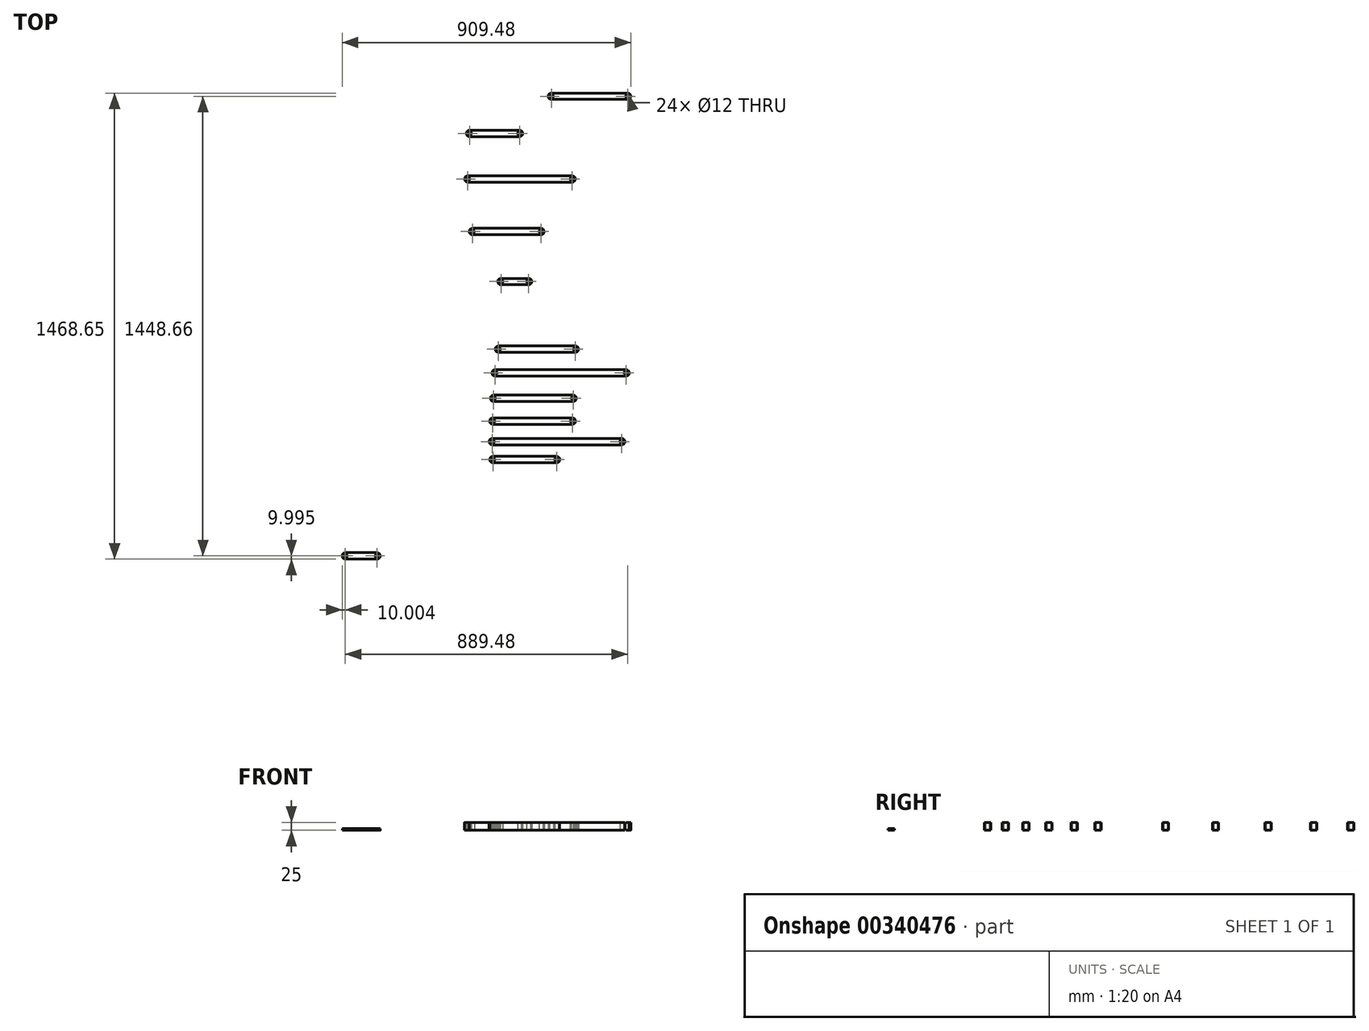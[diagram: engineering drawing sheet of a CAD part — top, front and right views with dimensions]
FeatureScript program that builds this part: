
annotation { "Feature Type Name" : "Feature", "Feature Type Description" : "" }
export const myFeature = defineFeature(function(context is Context, id is Id, definition is map)
    precondition{}
    {
        {
            var Q0;
            Q0=qCreatedBy(makeId("Top.planeOp"),FACE);
            var sketch = newSketch(context, id + "F0", { "sketchPlane" : qUnion([Q0])});
            skLineSegment(sketch, "E0", {"start": v(-54.16, 16.37) * mm, "end": v(146.43, 16.37) * mm, "construction": true});
            skCircle(sketch, "E1", {"center": v(-54.16, 16.37) * mm, "radius": 6 * mm});
            skCircle(sketch, "E2", {"center": v(146.43, 16.37) * mm, "radius": 6 * mm});
            skArc(sketch, "E3.0.startCap", {"start": v(-54.16, 6.37) * mm, "mid": v(-64.16, 16.37) * mm, "end": v(-54.16, 26.37) * mm});
            skArc(sketch, "E3.0.endCap", {"start": v(146.43, 26.37) * mm, "mid": v(156.43, 16.37) * mm, "end": v(146.43, 6.37) * mm});
            skLineSegment(sketch, "E3.0.left", {"start": v(-54.16, 26.37) * mm, "end": v(146.43, 26.37) * mm});
            skLineSegment(sketch, "E3.0.right", {"start": v(-54.16, 6.37) * mm, "end": v(146.43, 6.37) * mm});
            skSolve(sketch);
        }
        {
            var Q0;
            Q0=makeQuery(id+"F0.imprint","IMPRINT",FACE,{"disambiguationData":[TD([[makeQuery(id+"F0.imprint","IMPRINT",EDGE,{"derivedFrom":sQuery(id+"F0.wireOp",EDGE,"E1")}),-1.0]])]});
            extrude(context, id + "F1", {"entities" : qUnion([Q0]), "depth" : 25 * mm});
        }
        {
            var Q0;
            Q0=qCreatedBy(makeId("Top.planeOp"),FACE);
            var sketch = newSketch(context, id + "F2", { "sketchPlane" : qUnion([Q0])});
            skLineSegment(sketch, "E4", {"start": v(-56, 72.91) * mm, "end": v(351.89, 72.91) * mm, "construction": true});
            skCircle(sketch, "E5", {"center": v(-56, 72.91) * mm, "radius": 6 * mm});
            skCircle(sketch, "E6", {"center": v(351.89, 72.91) * mm, "radius": 6 * mm});
            skArc(sketch, "E7.0.startCap", {"start": v(-56, 62.91) * mm, "mid": v(-66, 72.91) * mm, "end": v(-56, 82.91) * mm});
            skArc(sketch, "E7.0.endCap", {"start": v(351.89, 82.91) * mm, "mid": v(361.89, 72.91) * mm, "end": v(351.89, 62.91) * mm});
            skLineSegment(sketch, "E7.0.left", {"start": v(-56, 82.91) * mm, "end": v(351.89, 82.91) * mm});
            skLineSegment(sketch, "E7.0.right", {"start": v(-56, 62.91) * mm, "end": v(351.89, 62.91) * mm});
            skSolve(sketch);
        }
        {
            var Q0;
            Q0 = qSketchRegion(id + "F2", true);
            extrude(context, id + "F3", {"entities" : qUnion([Q0]), "depth" : 25 * mm});
        }
        {
            var Q0;
            Q0=qCreatedBy(makeId("Top.planeOp"),FACE);
            var sketch = newSketch(context, id + "F4", { "sketchPlane" : qUnion([Q0])});
            skLineSegment(sketch, "E8", {"start": v(-54.66, 137.47) * mm, "end": v(195.94, 137.47) * mm, "construction": true});
            skCircle(sketch, "E9", {"center": v(-54.66, 137.47) * mm, "radius": 6 * mm});
            skCircle(sketch, "E10", {"center": v(195.94, 137.47) * mm, "radius": 6 * mm});
            skArc(sketch, "E11.0.startCap", {"start": v(-54.66, 127.47) * mm, "mid": v(-64.66, 137.47) * mm, "end": v(-54.66, 147.47) * mm});
            skArc(sketch, "E11.0.endCap", {"start": v(195.94, 147.47) * mm, "mid": v(205.94, 137.47) * mm, "end": v(195.94, 127.47) * mm});
            skLineSegment(sketch, "E11.0.left", {"start": v(-54.66, 147.47) * mm, "end": v(195.94, 147.47) * mm});
            skLineSegment(sketch, "E11.0.right", {"start": v(-54.66, 127.47) * mm, "end": v(195.94, 127.47) * mm});
            skSolve(sketch);
        }
        {
            var Q0;
            Q0 = qSketchRegion(id + "F4", true);
            extrude(context, id + "F5", {"entities" : qUnion([Q0]), "depth" : 25 * mm});
        }
        {
            var Q0;
            Q0=qCreatedBy(makeId("Top.planeOp"),FACE);
            var sketch = newSketch(context, id + "F6", { "sketchPlane" : qUnion([Q0])});
            skLineSegment(sketch, "E12", {"start": v(-52, 209.5) * mm, "end": v(198.6, 209.5) * mm, "construction": true});
            skCircle(sketch, "E13", {"center": v(-52, 209.5) * mm, "radius": 6 * mm});
            skCircle(sketch, "E14", {"center": v(198.6, 209.5) * mm, "radius": 6 * mm});
            skArc(sketch, "E15.0.startCap", {"start": v(-52, 199.5) * mm, "mid": v(-62, 209.5) * mm, "end": v(-52, 219.5) * mm});
            skArc(sketch, "E15.0.endCap", {"start": v(198.6, 219.5) * mm, "mid": v(208.6, 209.5) * mm, "end": v(198.6, 199.5) * mm});
            skLineSegment(sketch, "E15.0.left", {"start": v(-52, 219.5) * mm, "end": v(198.6, 219.5) * mm});
            skLineSegment(sketch, "E15.0.right", {"start": v(-52, 199.5) * mm, "end": v(198.6, 199.5) * mm});
            skSolve(sketch);
        }
        {
            var Q0;
            Q0 = qSketchRegion(id + "F6", true);
            extrude(context, id + "F7", {"entities" : qUnion([Q0]), "depth" : 25 * mm});
        }
        {
            var Q0;
            Q0=qCreatedBy(makeId("Top.planeOp"),FACE);
            var sketch = newSketch(context, id + "F8", { "sketchPlane" : qUnion([Q0])});
            skLineSegment(sketch, "E16", {"start": v(-47.32, 289.42) * mm, "end": v(365.4, 289.42) * mm, "construction": true});
            skCircle(sketch, "E17", {"center": v(-47.32, 289.42) * mm, "radius": 6 * mm});
            skCircle(sketch, "E18", {"center": v(365.4, 289.42) * mm, "radius": 6 * mm});
            skArc(sketch, "E19.0.startCap", {"start": v(-47.32, 279.42) * mm, "mid": v(-57.32, 289.42) * mm, "end": v(-47.32, 299.42) * mm});
            skArc(sketch, "E19.0.endCap", {"start": v(365.4, 299.42) * mm, "mid": v(375.4, 289.42) * mm, "end": v(365.4, 279.42) * mm});
            skLineSegment(sketch, "E19.0.left", {"start": v(-47.32, 299.42) * mm, "end": v(365.4, 299.42) * mm});
            skLineSegment(sketch, "E19.0.right", {"start": v(-47.32, 279.42) * mm, "end": v(365.4, 279.42) * mm});
            skSolve(sketch);
        }
        {
            var Q0;
            Q0 = qSketchRegion(id + "F8", true);
            extrude(context, id + "F9", {"entities" : qUnion([Q0]), "depth" : 25 * mm});
        }
        {
            var Q0;
            Q0=qCreatedBy(makeId("Top.planeOp"),FACE);
            var sketch = newSketch(context, id + "F10", { "sketchPlane" : qUnion([Q0])});
            skLineSegment(sketch, "E20", {"start": v(-36.71, 364.39) * mm, "end": v(205.52, 364.39) * mm, "construction": true});
            skCircle(sketch, "E21", {"center": v(-36.71, 364.39) * mm, "radius": 6 * mm});
            skCircle(sketch, "E22", {"center": v(205.52, 364.39) * mm, "radius": 6 * mm});
            skArc(sketch, "E23.0.startCap", {"start": v(-36.71, 354.39) * mm, "mid": v(-46.71, 364.39) * mm, "end": v(-36.71, 374.39) * mm});
            skArc(sketch, "E23.0.endCap", {"start": v(205.52, 374.39) * mm, "mid": v(215.52, 364.39) * mm, "end": v(205.52, 354.39) * mm});
            skLineSegment(sketch, "E23.0.left", {"start": v(-36.71, 374.39) * mm, "end": v(205.52, 374.39) * mm});
            skLineSegment(sketch, "E23.0.right", {"start": v(-36.71, 354.39) * mm, "end": v(205.52, 354.39) * mm});
            skSolve(sketch);
        }
        {
            var Q0;
            Q0 = qSketchRegion(id + "F10", true);
            extrude(context, id + "F11", {"entities" : qUnion([Q0]), "depth" : 25 * mm});
        }
        {
            var Q0;
            Q0=qCreatedBy(makeId("Top.planeOp"),FACE);
            var sketch = newSketch(context, id + "F12", { "sketchPlane" : qUnion([Q0])});
            skLineSegment(sketch, "E24", {"start": v(-519.27, -287.23) * mm, "end": v(-419.27, -287.23) * mm, "construction": true});
            skCircle(sketch, "E25", {"center": v(-519.27, -287.23) * mm, "radius": 6 * mm});
            skCircle(sketch, "E26", {"center": v(-419.27, -287.23) * mm, "radius": 6 * mm});
            skArc(sketch, "E27.0.startCap", {"start": v(-519.27, -297.23) * mm, "mid": v(-529.27, -287.23) * mm, "end": v(-519.27, -277.23) * mm});
            skArc(sketch, "E27.0.endCap", {"start": v(-419.27, -277.23) * mm, "mid": v(-409.27, -287.23) * mm, "end": v(-419.27, -297.23) * mm});
            skLineSegment(sketch, "E27.0.left", {"start": v(-519.27, -277.23) * mm, "end": v(-419.27, -277.23) * mm});
            skLineSegment(sketch, "E27.0.right", {"start": v(-519.27, -297.23) * mm, "end": v(-419.27, -297.23) * mm});
            skSolve(sketch);
        }
        {
            var Q0;
            Q0 = qSketchRegion(id + "F12", true);
            extrude(context, id + "F13", {"entities" : qUnion([Q0]), "depth" : 5 * mm});
        }
        {
            var Q0;
            Q0=qCreatedBy(makeId("Top.planeOp"),FACE);
            var sketch = newSketch(context, id + "F14", { "sketchPlane" : qUnion([Q0])});
            skLineSegment(sketch, "E28", {"start": v(-28.92, 577.47) * mm, "end": v(58.18, 577.47) * mm, "construction": true});
            skCircle(sketch, "E29", {"center": v(-28.92, 577.47) * mm, "radius": 6 * mm});
            skCircle(sketch, "E30", {"center": v(58.18, 577.47) * mm, "radius": 6 * mm});
            skArc(sketch, "E31.0.startCap", {"start": v(-28.92, 567.47) * mm, "mid": v(-38.92, 577.47) * mm, "end": v(-28.92, 587.47) * mm});
            skArc(sketch, "E31.0.endCap", {"start": v(58.18, 587.47) * mm, "mid": v(68.18, 577.47) * mm, "end": v(58.18, 567.47) * mm});
            skLineSegment(sketch, "E31.0.left", {"start": v(-28.92, 587.47) * mm, "end": v(58.18, 587.47) * mm});
            skLineSegment(sketch, "E31.0.right", {"start": v(-28.92, 567.47) * mm, "end": v(58.18, 567.47) * mm});
            skSolve(sketch);
        }
        {
            var Q0;
            Q0 = qSketchRegion(id + "F14", true);
            extrude(context, id + "F15", {"entities" : qUnion([Q0]), "depth" : 25 * mm});
        }
        {
            var Q0;
            Q0=qCreatedBy(makeId("Top.planeOp"),FACE);
            var sketch = newSketch(context, id + "F16", { "sketchPlane" : qUnion([Q0])});
            skLineSegment(sketch, "E32", {"start": v(-118.76, 734.99) * mm, "end": v(97.37, 734.99) * mm, "construction": true});
            skCircle(sketch, "E33", {"center": v(-118.76, 734.99) * mm, "radius": 6 * mm});
            skCircle(sketch, "E34", {"center": v(97.37, 734.99) * mm, "radius": 6 * mm});
            skArc(sketch, "E35.0.startCap", {"start": v(-118.76, 724.99) * mm, "mid": v(-128.76, 734.99) * mm, "end": v(-118.76, 744.99) * mm});
            skArc(sketch, "E35.0.endCap", {"start": v(97.37, 744.99) * mm, "mid": v(107.37, 734.99) * mm, "end": v(97.37, 724.99) * mm});
            skLineSegment(sketch, "E35.0.left", {"start": v(-118.76, 744.99) * mm, "end": v(97.37, 744.99) * mm});
            skLineSegment(sketch, "E35.0.right", {"start": v(-118.76, 724.99) * mm, "end": v(97.37, 724.99) * mm});
            skSolve(sketch);
        }
        {
            var Q0;
            Q0 = qSketchRegion(id + "F16", true);
            extrude(context, id + "F17", {"entities" : qUnion([Q0]), "depth" : 25 * mm});
        }
        {
            var Q0;
            Q0=qCreatedBy(makeId("Top.planeOp"),FACE);
            var sketch = newSketch(context, id + "F18", { "sketchPlane" : qUnion([Q0])});
            skLineSegment(sketch, "E36", {"start": v(-133.44, 900.73) * mm, "end": v(195.23, 900.73) * mm, "construction": true});
            skCircle(sketch, "E37", {"center": v(-133.44, 900.73) * mm, "radius": 6 * mm});
            skCircle(sketch, "E38", {"center": v(195.23, 900.73) * mm, "radius": 6 * mm});
            skArc(sketch, "E39.0.startCap", {"start": v(-133.44, 890.73) * mm, "mid": v(-143.44, 900.73) * mm, "end": v(-133.44, 910.73) * mm});
            skArc(sketch, "E39.0.endCap", {"start": v(195.23, 910.73) * mm, "mid": v(205.23, 900.73) * mm, "end": v(195.23, 890.73) * mm});
            skLineSegment(sketch, "E39.0.left", {"start": v(-133.44, 910.73) * mm, "end": v(195.23, 910.73) * mm});
            skLineSegment(sketch, "E39.0.right", {"start": v(-133.44, 890.73) * mm, "end": v(195.23, 890.73) * mm});
            skSolve(sketch);
        }
        {
            var Q0;
            Q0 = qSketchRegion(id + "F18", true);
            extrude(context, id + "F19", {"entities" : qUnion([Q0]), "depth" : 25 * mm});
        }
        {
            var Q0;
            Q0=qCreatedBy(makeId("Top.planeOp"),FACE);
            var sketch = newSketch(context, id + "F20", { "sketchPlane" : qUnion([Q0])});
            skLineSegment(sketch, "E40", {"start": v(-127.87, 1044.3) * mm, "end": v(29.64, 1044.3) * mm, "construction": true});
            skCircle(sketch, "E41", {"center": v(-127.87, 1044.3) * mm, "radius": 6 * mm});
            skCircle(sketch, "E42", {"center": v(29.64, 1044.3) * mm, "radius": 6 * mm});
            skArc(sketch, "E43.0.startCap", {"start": v(-127.87, 1034.3) * mm, "mid": v(-137.87, 1044.3) * mm, "end": v(-127.87, 1054.3) * mm});
            skArc(sketch, "E43.0.endCap", {"start": v(29.64, 1054.3) * mm, "mid": v(39.64, 1044.3) * mm, "end": v(29.64, 1034.3) * mm});
            skLineSegment(sketch, "E43.0.left", {"start": v(-127.87, 1054.3) * mm, "end": v(29.64, 1054.3) * mm});
            skLineSegment(sketch, "E43.0.right", {"start": v(-127.87, 1034.3) * mm, "end": v(29.64, 1034.3) * mm});
            skSolve(sketch);
        }
        {
            var Q0;
            Q0 = qSketchRegion(id + "F20", true);
            extrude(context, id + "F21", {"entities" : qUnion([Q0]), "depth" : 25 * mm});
        }
        {
            var Q0;
            Q0=qCreatedBy(makeId("Top.planeOp"),FACE);
            var sketch = newSketch(context, id + "F22", { "sketchPlane" : qUnion([Q0])});
            skLineSegment(sketch, "E44", {"start": v(130.21, 1161.42) * mm, "end": v(370.21, 1161.42) * mm, "construction": true});
            skCircle(sketch, "E45", {"center": v(130.21, 1161.42) * mm, "radius": 6 * mm});
            skCircle(sketch, "E46", {"center": v(370.21, 1161.42) * mm, "radius": 6 * mm});
            skArc(sketch, "E47.0.startCap", {"start": v(130.21, 1151.42) * mm, "mid": v(120.21, 1161.42) * mm, "end": v(130.21, 1171.42) * mm});
            skArc(sketch, "E47.0.endCap", {"start": v(370.21, 1171.42) * mm, "mid": v(380.21, 1161.42) * mm, "end": v(370.21, 1151.42) * mm});
            skLineSegment(sketch, "E47.0.left", {"start": v(130.21, 1171.42) * mm, "end": v(370.21, 1171.42) * mm});
            skLineSegment(sketch, "E47.0.right", {"start": v(130.21, 1151.42) * mm, "end": v(370.21, 1151.42) * mm});
            skSolve(sketch);
        }
        {
            var Q0;
            Q0 = qSketchRegion(id + "F22", true);
            extrude(context, id + "F23", {"entities" : qUnion([Q0]), "depth" : 25 * mm});
        }
    });
